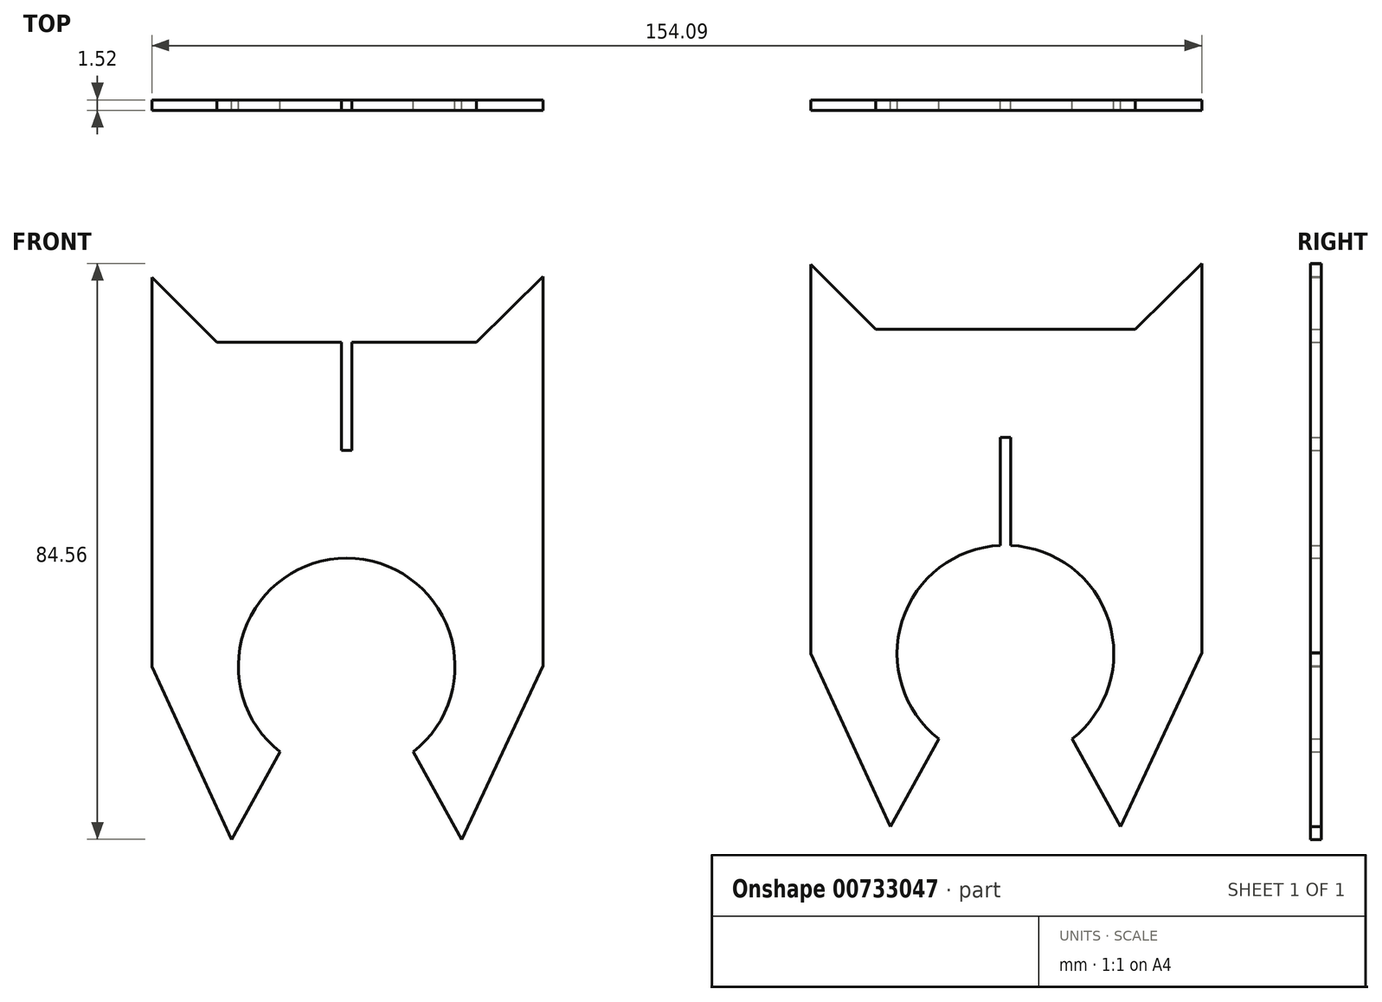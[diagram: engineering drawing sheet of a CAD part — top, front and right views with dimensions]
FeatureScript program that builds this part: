
annotation { "Feature Type Name" : "Feature", "Feature Type Description" : "" }
export const myFeature = defineFeature(function(context is Context, id is Id, definition is map)
    precondition{}
    {
        {
            var Q0;
            Q0=qCreatedBy(makeId("Front.planeOp"),FACE);
            var sketch = newSketch(context, id + "F0", { "sketchPlane" : qUnion([Q0])});
            skArc(sketch, "E0", {"start": v(-380.26, -0.74) * mm, "mid": v(-390.04, 27.7) * mm, "end": v(-399.82, -0.74) * mm});
            skLineSegment(sketch, "E1", {"start": v(-399.82, -0.74) * mm, "end": v(-406.94, -13.58) * mm});
            skLineSegment(sketch, "E2", {"start": v(-380.26, -0.74) * mm, "end": v(-373.14, -13.58) * mm});
            skLineSegment(sketch, "E3", {"start": v(-418.62, 11.8) * mm, "end": v(-418.62, 68.95) * mm});
            skLineSegment(sketch, "E4", {"start": v(-361.23, 69.08) * mm, "end": v(-361.23, 11.93) * mm});
            skLineSegment(sketch, "E5.left", {"start": v(-418.62, 68.95) * mm, "end": v(-418.62, 59.43) * mm});
            skLineSegment(sketch, "E6.left", {"start": v(-361.23, 69.08) * mm, "end": v(-361.23, 59.56) * mm});
            skLineSegment(sketch, "E7", {"start": v(-418.62, 68.95) * mm, "end": v(-409.1, 59.43) * mm});
            skLineSegment(sketch, "E8", {"start": v(-371, 59.43) * mm, "end": v(-361.23, 69.08) * mm});
            skLineSegment(sketch, "E9", {"start": v(-409.1, 59.43) * mm, "end": v(-390.8, 59.43) * mm});
            skPoint(sketch, "E10.orphan", {"position": v(-390.04, 18.15) * mm});
            skPoint(sketch, "E11.end.orphan", {"position": v(-390.04, 5.45) * mm});
            skLineSegment(sketch, "E12", {"start": v(-361.23, 11.93) * mm, "end": v(-373.14, -13.58) * mm});
            skLineSegment(sketch, "E13", {"start": v(-418.62, 11.8) * mm, "end": v(-406.94, -13.58) * mm});
            skPoint(sketch, "E14.orphan", {"position": v(-396.4, 18.15) * mm});
            skPoint(sketch, "E15.right.start.orphan", {"position": v(-383.7, 18.15) * mm});
            skPoint(sketch, "E16.orphan", {"position": v(-396.4, 5.45) * mm});
            skPoint(sketch, "E17.orphan", {"position": v(-383.7, 5.45) * mm});
            skPoint(sketch, "E18.start.orphan", {"position": v(-419.12, -35.55) * mm});
            skLineSegment(sketch, "E19", {"start": v(-390.04, 11.8) * mm, "end": v(-390.04, -31.79) * mm, "construction": true});
            skPoint(sketch, "E20.orphan", {"position": v(-390.04, 59.43) * mm});
            skArc(sketch, "E21", {"start": v(-283.56, 1.16) * mm, "mid": v(-278.18, 18.51) * mm, "end": v(-292.57, 29.59) * mm});
            skLineSegment(sketch, "E22", {"start": v(-303.12, 1.16) * mm, "end": v(-310.24, -11.68) * mm});
            skLineSegment(sketch, "E23", {"start": v(-283.56, 1.16) * mm, "end": v(-276.43, -11.68) * mm});
            skLineSegment(sketch, "E24", {"start": v(-321.91, 13.7) * mm, "end": v(-321.91, 70.85) * mm});
            skLineSegment(sketch, "E25", {"start": v(-264.53, 70.98) * mm, "end": v(-264.53, 13.83) * mm});
            skLineSegment(sketch, "E26.left", {"start": v(-321.91, 70.85) * mm, "end": v(-321.91, 61.33) * mm});
            skLineSegment(sketch, "E27.left", {"start": v(-264.53, 70.98) * mm, "end": v(-264.53, 61.45) * mm});
            skLineSegment(sketch, "E28", {"start": v(-321.91, 70.85) * mm, "end": v(-312.39, 61.33) * mm});
            skLineSegment(sketch, "E29", {"start": v(-274.29, 61.33) * mm, "end": v(-264.53, 70.98) * mm});
            skLineSegment(sketch, "E30", {"start": v(-312.39, 61.33) * mm, "end": v(-274.29, 61.33) * mm});
            skPoint(sketch, "E31.orphan", {"position": v(-293.34, 20.05) * mm});
            skPoint(sketch, "E32.end.orphan", {"position": v(-293.34, 7.35) * mm});
            skLineSegment(sketch, "E33", {"start": v(-264.53, 13.83) * mm, "end": v(-276.43, -11.68) * mm});
            skLineSegment(sketch, "E34", {"start": v(-321.91, 13.7) * mm, "end": v(-310.24, -11.68) * mm});
            skPoint(sketch, "E35.orphan", {"position": v(-299.69, 20.05) * mm});
            skPoint(sketch, "E36.right.start.orphan", {"position": v(-286.99, 20.05) * mm});
            skPoint(sketch, "E37.orphan", {"position": v(-299.69, 7.35) * mm});
            skPoint(sketch, "E38.orphan", {"position": v(-286.99, 7.35) * mm});
            skPoint(sketch, "E39.start.orphan", {"position": v(-322.41, -33.65) * mm});
            skLineSegment(sketch, "E40", {"start": v(-293.34, 13.7) * mm, "end": v(-293.34, -29.89) * mm, "construction": true});
            skPoint(sketch, "E41.orphan", {"position": v(-293.34, 61.33) * mm});
            skLineSegment(sketch, "E42", {"start": v(-390.04, 43.55) * mm, "end": v(-389.28, 43.55) * mm});
            skLineSegment(sketch, "E43", {"start": v(-389.28, 43.55) * mm, "end": v(-389.28, 59.43) * mm});
            skLineSegment(sketch, "E44.MirrorCS", {"start": v(-390.8, 43.55) * mm, "end": v(-390.8, 59.43) * mm});
            skLineSegment(sketch, "E45", {"start": v(-390.04, 43.55) * mm, "end": v(-390.8, 43.55) * mm});
            skLineSegment(sketch, "E46.trimOffspring", {"start": v(-389.28, 59.43) * mm, "end": v(-371, 59.43) * mm});
            skLineSegment(sketch, "E47", {"start": v(-293.34, 61.33) * mm, "end": v(-293.34, 45.45) * mm, "construction": true});
            skLineSegment(sketch, "E48", {"start": v(-292.57, 29.59) * mm, "end": v(-292.57, 45.45) * mm});
            skLineSegment(sketch, "E49", {"start": v(-292.57, 45.45) * mm, "end": v(-293.34, 45.45) * mm});
            skLineSegment(sketch, "E50.MirrorCS", {"start": v(-294.1, 29.59) * mm, "end": v(-294.1, 45.45) * mm});
            skLineSegment(sketch, "E51.MirrorCS", {"start": v(-294.1, 45.45) * mm, "end": v(-293.34, 45.45) * mm});
            skArc(sketch, "E52.trimOffspring", {"start": v(-294.1, 29.59) * mm, "mid": v(-308.5, 18.51) * mm, "end": v(-303.12, 1.16) * mm});
            skSolve(sketch);
        }
        {
            var Q0;
            Q0=makeQuery(id+"F0.imprint","IMPRINT",FACE,{"disambiguationData":[TD([[makeQuery(id+"F0.imprint","IMPRINT",EDGE,{"derivedFrom":sQuery(id+"F0.wireOp",EDGE,"E0")}),-1.0]])]});
            var Q1;
            Q1=makeQuery(id+"F0.imprint","IMPRINT",FACE,{"disambiguationData":[TD([[makeQuery(id+"F0.imprint","IMPRINT",EDGE,{"derivedFrom":sQuery(id+"F0.wireOp",EDGE,"61ae4a59-eb16-45d4-b016-934e2b11c005")}),-1.0]])]});
            var Q2;
            Q2=makeQuery(id+"F0.imprint","IMPRINT",FACE,{"disambiguationData":[TD([[makeQuery(id+"F0.imprint","IMPRINT",EDGE,{"derivedFrom":sQuery(id+"F0.wireOp",EDGE,"lthowKyj-tcvS-riK4-30w2-RtNUSL9raJIq")}),-1.0]])]});
            var Q3;
            Q3=makeQuery(id+"F0.imprint","IMPRINT",FACE,{"disambiguationData":[TD([[makeQuery(id+"F0.imprint","IMPRINT",EDGE,{"derivedFrom":sQuery(id+"F0.wireOp",EDGE,"E21")}),-1.0]])]});
            extrude(context, id + "F1", {"entities" : qUnion([Q0, Q1, Q2, Q3]), "depth" : 1.52 * mm, "offsetDistance" : 25.4 * mm});
        }
    });
